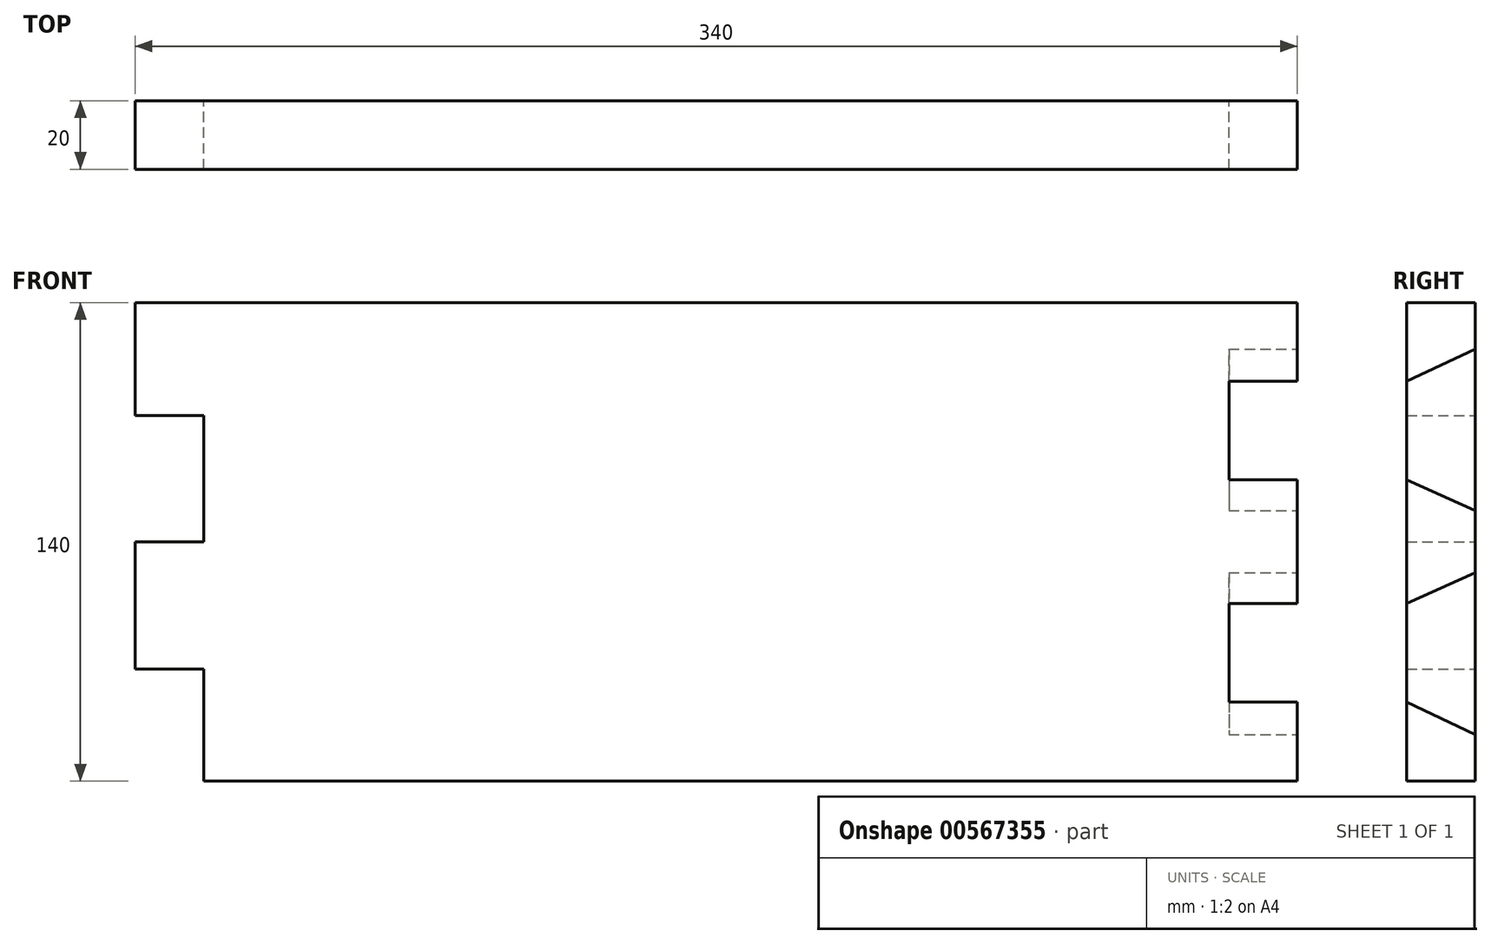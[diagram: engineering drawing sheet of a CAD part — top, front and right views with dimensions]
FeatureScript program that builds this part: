
annotation { "Feature Type Name" : "Feature", "Feature Type Description" : "" }
export const myFeature = defineFeature(function(context is Context, id is Id, definition is map)
    precondition{}
    {
        {
            var Q0;
            Q0=qCreatedBy(makeId("Front.planeOp"),FACE);
            var sketch = newSketch(context, id + "F0", { "sketchPlane" : qUnion([Q0])});
            skLineSegment(sketch, "E0.bottom", {"start": v(-199.46, 107.23) * mm, "end": v(140.54, 107.23) * mm});
            skLineSegment(sketch, "E0.top", {"start": v(-179.46, -32.77) * mm, "end": v(140.54, -32.77) * mm});
            skLineSegment(sketch, "E0.right", {"start": v(140.54, 107.23) * mm, "end": v(140.54, -32.77) * mm});
            skLineSegment(sketch, "E1.bottom", {"start": v(-199.46, 107.23) * mm, "end": v(-179.46, 107.23) * mm});
            skLineSegment(sketch, "E1.left", {"start": v(-199.46, 107.23) * mm, "end": v(-199.46, 74.17) * mm});
            skLineSegment(sketch, "E2.bottom", {"start": v(-199.46, 0) * mm, "end": v(-179.46, 0) * mm});
            skLineSegment(sketch, "E2.right", {"start": v(-179.46, 0) * mm, "end": v(-179.46, -32.77) * mm});
            skLineSegment(sketch, "E3.bottom", {"start": v(-199.46, 37.23) * mm, "end": v(-179.46, 37.23) * mm});
            skLineSegment(sketch, "E3.left", {"start": v(-199.46, 37.23) * mm, "end": v(-199.46, 0) * mm});
            skLineSegment(sketch, "E4.bottom", {"start": v(-199.46, 74.17) * mm, "end": v(-179.46, 74.17) * mm});
            skLineSegment(sketch, "E4.right", {"start": v(-179.46, 74.17) * mm, "end": v(-179.46, 37.23) * mm});
            skPoint(sketch, "E5.orphan", {"position": v(-199.46, -32.77) * mm});
            skLineSegment(sketch, "E6", {"start": v(-179.46, 37.23) * mm, "end": v(-179.46, 0) * mm});
            skLineSegment(sketch, "E7", {"start": v(-179.46, 18.62) * mm, "end": v(-199.46, 18.62) * mm});
            skPoint(sketch, "E8", {"position": v(-189.46, 18.62) * mm});
            skSolve(sketch);
        }
        {
            var Q0;
            Q0=makeQuery(id+"F0.imprint","IMPRINT",FACE,{"disambiguationData":[TD([[makeQuery(id+"F0.imprint","IMPRINT",EDGE,{"derivedFrom":sQuery(id+"F0.wireOp",EDGE,"E0.bottom")}),-1.0]])]});
            var Q1;
            {var subQ0=sQuery(id+"F0.wireOp",EDGE,"E3.bottom");Q1=makeQuery(id+"F0.imprint","IMPRINT",FACE,{"disambiguationData":[TD([[makeQuery(id+"F0.imprint","IMPRINT",EDGE,{"derivedFrom":subQ0}),-1.0]])]});}
            var Q2;
            {var subQ0=sQuery(id+"F0.wireOp",EDGE,"E2.bottom");Q2=makeQuery(id+"F0.imprint","IMPRINT",FACE,{"disambiguationData":[TD([[makeQuery(id+"F0.imprint","IMPRINT",EDGE,{"derivedFrom":subQ0}),1.0]])]});}
            extrude(context, id + "F1", {"entities" : qUnion([Q0, Q1, Q2]), "depth" : 20 * mm, "offsetDistance" : 25.4 * mm});
        }
        {
            var Q0;
            Q0=makeQuery(id+"F1.opExtrude","SWEPT_FACE",FACE,{"disambiguationData":[OSD([sQuery(id+"F0.wireOp",EDGE,"E0.right")])]});
            var sketch = newSketch(context, id + "F2", { "sketchPlane" : qUnion([Q0])});
            skLineSegment(sketch, "E9", {"start": v(-20, 37.23) * mm, "end": v(0, 37.23) * mm});
            skLineSegment(sketch, "E10", {"start": v(-20, -9.68) * mm, "end": v(0, -19.14) * mm});
            skLineSegment(sketch, "E11", {"start": v(-20, 19.13) * mm, "end": v(0, 28.15) * mm});
            skLineSegment(sketch, "E12.MirrorCS", {"start": v(-20, 55.34) * mm, "end": v(0, 46.3) * mm});
            skLineSegment(sketch, "E13.MirrorCS", {"start": v(-20, 84.14) * mm, "end": v(0, 93.6) * mm});
            skSolve(sketch);
        }
        {
            var Q0;
            {var subQ0=sQuery(id+"F2.wireOp",EDGE,"E12.MirrorCS");Q0=makeQuery(id+"F2.imprint","IMPRINT",FACE,{"disambiguationData":[TD([[makeQuery(id+"F2.imprint","IMPRINT",EDGE,{"derivedFrom":subQ0}),1.0]])]});}
            var Q1;
            {var subQ0=sQuery(id+"F2.wireOp",EDGE,"E10");Q1=makeQuery(id+"F2.imprint","IMPRINT",FACE,{"disambiguationData":[TD([[makeQuery(id+"F2.imprint","IMPRINT",EDGE,{"derivedFrom":subQ0}),1.0]])]});}
            extrude(context, id + "F3", {"entities" : qUnion([Q0, Q1]), "operationType" : NewBodyOperationType.REMOVE, "oppositeDirection" : true, "depth" : 20 * mm, "offsetDistance" : 25 * mm});
        }
    });
